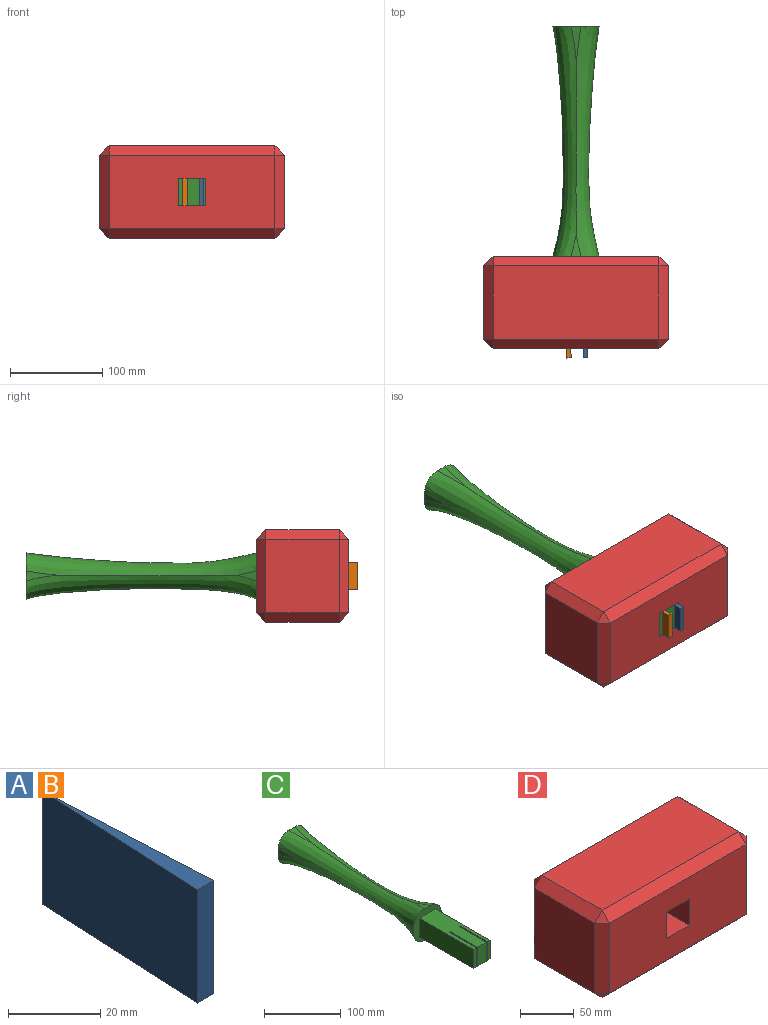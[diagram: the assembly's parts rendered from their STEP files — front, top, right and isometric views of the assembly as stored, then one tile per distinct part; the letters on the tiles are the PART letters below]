
ASSEMBLY  parts=4 mates=3
PART A: 5 faces, bbox 5x50x30 mm
  f0: plane 30x5mm, normal (0,-1,0), area 150mm2, adj f1,f2,f3,f4
  f1: plane 50x5mm, normal (0,0,1), area 125mm2, adj f0,f3,f4
  f2: plane 50x5mm, normal (0,0,-1), area 125mm2, adj f0,f3,f4
  f3: plane 50x30mm, normal (-1,0.05,0), area 1501.9mm2, adj f0,f1,f2,f4
  f4: plane 50x30mm, normal (1,0.05,0), area 1501.9mm2, adj f0,f1,f2,f3
PART B: same geometry as A
PART C: 27 faces, bbox 56.3x357.6x55.7 mm
  f0: plane 30x16mm, normal (0,-1,0), area 480mm2, adj f2,f18,f21,f25
  f1: plane 30x5mm, normal (0,-1,0), area 150mm2, adj f2,f18,f19,f22
  f2: plane 100x30mm, normal (0,0,1), area 2800mm2, adj f0,f1,f10,f17,f19,f20,f21,f22
  f3: extruded ~32.78x10.97mm, area 165.1mm2, adj f9,f13,f15
  f4: extruded ~22.27x12.56mm, area 143mm2, adj f10,f13,f14
  f5: extruded ~20.83x10.76mm, area 112.1mm2, adj f10,f14,f16
  f6: extruded ~38.21x10.58mm, area 183.3mm2, adj f9,f15,f16
  f7: extruded ~32.7x10.55mm, area 157.6mm2, adj f9,f14,f16
  f8: extruded ~20.74x11.38mm, area 119mm2, adj f10,f13,f15
  f9: plane 54.02x54.02mm, normal (0,1,0), area 2178.2mm2, adj f3,f6,f7,f11,f13,f14,f15,f16
  f10: plane 54.82x54.82mm, normal (0,-1,0), area 1287.1mm2, adj f2,f4,f5,f8,f12,f13,f14,f15
  f11: extruded ~38.36x11.8mm, area 208.6mm2, adj f9,f13,f14
  f12: extruded ~22.68x10.83mm, area 122.1mm2, adj f10,f15,f16
  f13: bspline ~254.87x31.38mm, area 7810.3mm2, adj f3,f4,f8,f9,f10,f11,f14,f15
  f14: bspline ~255.98x31.37mm, area 7818.5mm2, adj f4,f5,f7,f9,f10,f11,f13,f16
  f15: bspline ~254.52x31.32mm, area 7818.1mm2, adj f3,f6,f8,f9,f10,f12,f13,f16
  f16: bspline ~250.81x30.7mm, area 7822.4mm2, adj f5,f6,f7,f9,f10,f12,f14,f15
  f17: plane 100x30mm, normal (-1,0,0), area 3000mm2, adj f2,f10,f18,f20
  f18: plane 100x30mm, normal (0,0,-1), area 2800mm2, adj f0,f1,f10,f17,f19,f20,f21,f22
  f19: plane 100x30mm, normal (1,0,0), area 3000mm2, adj f1,f2,f10,f18
  f20: plane 30x5mm, normal (0,-1,0), area 150mm2, adj f2,f17,f18,f24
  f21: plane 50x30mm, normal (1,0,0), area 1500mm2, adj f0,f2,f18,f23
  f22: plane 50x30mm, normal (-1,0,0), area 1500mm2, adj f1,f2,f18,f23
  f23: plane 30x2mm, normal (0,-1,0), area 60mm2, adj f2,f18,f21,f22
  f24: plane 50x30mm, normal (1,0,0), area 1500mm2, adj f2,f18,f20,f26
  f25: plane 50x30mm, normal (-1,0,0), area 1500mm2, adj f0,f2,f18,f26
  f26: plane 30x2mm, normal (0,-1,0), area 60mm2, adj f2,f18,f24,f25
PART D: 30 faces, bbox 200x100x100 mm
  f0: plane 180x80mm, normal (0,-1,0), area 13500mm2, adj f6,f10,f11,f12,f26,f27,f28,f29
  f1: plane 180x80mm, normal (0,1,0), area 13500mm2, adj f14,f19,f22,f25,f26,f27,f28,f29
  f2: plane 80x80mm, normal (-1,0,0), area 6400mm2, adj f11,f20,f21,f25
  f3: plane 80x80mm, normal (1,0,0), area 6400mm2, adj f6,f9,f13,f14
  f4: plane 180x80mm, normal (0,0,1), area 14400mm2, adj f9,f10,f19,f20
  f5: plane 180x80mm, normal (0,0,-1), area 14400mm2, adj f12,f13,f21,f22
  f6: plane 80x10mm, normal (0.71,-0.71,0), area 1131.4mm2, adj f0,f3,f7,f8
  f7: plane 10x10mm, normal (0.58,-0.58,0.58), area 86.6mm2, adj f6,f9,f10
  f8: plane 10x10mm, normal (0.58,-0.58,-0.58), area 86.6mm2, adj f6,f12,f13
  f9: plane 80x10mm, normal (0.71,0,0.71), area 1131.4mm2, adj f3,f4,f7,f15
  f10: plane 180x10mm, normal (0,-0.71,0.71), area 2545.6mm2, adj f0,f4,f7,f16
  f11: plane 80x10mm, normal (-0.71,-0.71,0), area 1131.4mm2, adj f0,f2,f16,f17
  f12: plane 180x10mm, normal (0,-0.71,-0.71), area 2545.6mm2, adj f0,f5,f8,f17
  f13: plane 80x10mm, normal (0.71,0,-0.71), area 1131.4mm2, adj f3,f5,f8,f18
  f14: plane 80x10mm, normal (0.71,0.71,0), area 1131.4mm2, adj f1,f3,f15,f18
  f15: plane 10x10mm, normal (0.58,0.58,0.58), area 86.6mm2, adj f9,f14,f19
  f16: plane 10x10mm, normal (-0.58,-0.58,0.58), area 86.6mm2, adj f10,f11,f20
  f17: plane 10x10mm, normal (-0.58,-0.58,-0.58), area 86.6mm2, adj f11,f12,f21
  f18: plane 10x10mm, normal (0.58,0.58,-0.58), area 86.6mm2, adj f13,f14,f22
  f19: plane 180x10mm, normal (0,0.71,0.71), area 2545.6mm2, adj f1,f4,f15,f23
  f20: plane 80x10mm, normal (-0.71,0,0.71), area 1131.4mm2, adj f2,f4,f16,f23
  f21: plane 80x10mm, normal (-0.71,0,-0.71), area 1131.4mm2, adj f2,f5,f17,f24
  f22: plane 180x10mm, normal (0,0.71,-0.71), area 2545.6mm2, adj f1,f5,f18,f24
  f23: plane 10x10mm, normal (-0.58,0.58,0.58), area 86.6mm2, adj f19,f20,f25
  f24: plane 10x10mm, normal (-0.58,0.58,-0.58), area 86.6mm2, adj f21,f22,f25
  f25: plane 80x10mm, normal (-0.71,0.71,0), area 1131.4mm2, adj f1,f2,f23,f24
  f26: plane 100x30mm, normal (0,0,1), area 3000mm2, adj f0,f1,f27,f29
  f27: plane 100x30mm, normal (-1,0,0), area 3000mm2, adj f0,f1,f26,f28
  f28: plane 100x30mm, normal (0,0,-1), area 3000mm2, adj f0,f1,f27,f29
  f29: plane 100x30mm, normal (1,0,0), area 3000mm2, adj f0,f1,f26,f28
PLACE A rot(axis=(0,0,1),2.9deg) t=(-194.05,67.43,30.5)mm
PLACE B rot(axis=(0,0,1),2.9deg) t=(-212.05,67.43,30.5)mm
PLACE C t=(-83.86,52.76,20.5)mm
PLACE D t=(-314.76,-95.36,-4.5)mm
MATE parallel A.f3 <-> C.f21  axis (-1,0,0) through (-118.9,-120.25,30.5)mm
MATE parallel B.f3 <-> C.f24  axis (-1,0,0) through (-136.9,-120.25,30.5)mm
MATE parallel D.f1 <-> C.f10  axis (0,1,0) through (-111.9,-10.25,60.5)mm
